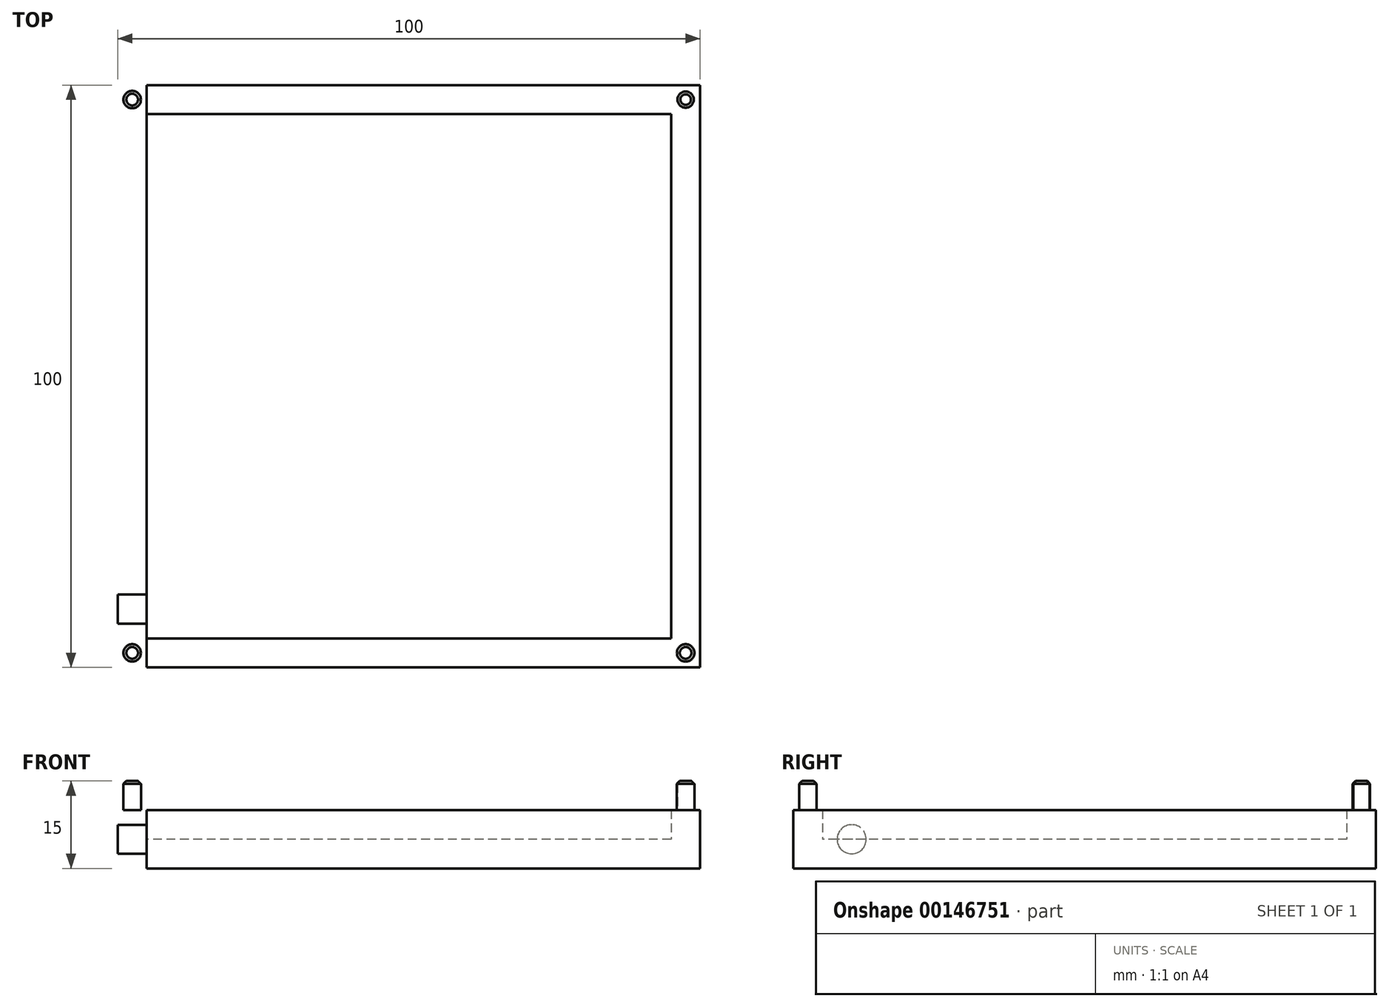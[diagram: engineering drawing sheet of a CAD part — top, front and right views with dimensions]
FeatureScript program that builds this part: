
annotation { "Feature Type Name" : "Feature", "Feature Type Description" : "" }
export const myFeature = defineFeature(function(context is Context, id is Id, definition is map)
    precondition{}
    {
        {
            var Q0;
            Q0=qCreatedBy(makeId("Top.planeOp"),FACE);
            var sketch = newSketch(context, id + "F0", { "sketchPlane" : qUnion([Q0])});
            skLineSegment(sketch, "E0.bottom", {"start": v(50, 50) * mm, "end": v(-50, 50) * mm});
            skLineSegment(sketch, "E0.top", {"start": v(50, -50) * mm, "end": v(-50, -50) * mm});
            skLineSegment(sketch, "E0.left", {"start": v(50, 50) * mm, "end": v(50, -50) * mm});
            skLineSegment(sketch, "E0.right", {"start": v(-50, 50) * mm, "end": v(-50, -50) * mm});
            skPoint(sketch, "E0.middle", {"position": v(0, 0) * mm});
            skSolve(sketch);
        }
        {
            var Q0;
            Q0=makeQuery(id+"F0.imprint","IMPRINT",FACE,{"disambiguationData":[TD([[makeQuery(id+"F0.imprint","IMPRINT",EDGE,{"derivedFrom":sQuery(id+"F0.wireOp",EDGE,"E0.bottom")}),1.0]])]});
            extrude(context, id + "F1", {"entities" : qUnion([Q0]), "depth" : 10 * mm});
        }
        {
            var Q0;
            Q0=makeQuery(id+"F1.opExtrude","CAP_FACE",FACE,{"disambiguationData":[OSD([sQuery(id+"F0.wireOp",EDGE,"E0.bottom"),sQuery(id+"F0.wireOp",EDGE,"E0.top"),sQuery(id+"F0.wireOp",EDGE,"E0.left"),sQuery(id+"F0.wireOp",EDGE,"E0.right")])],"isStart":false});
            shell(context, id + "F2", {"entities" : qUnion([Q0]), "thickness" : 5 * mm});
        }
        {
            var Q0;
            Q0=makeQuery(id+"F1.opExtrude","CAP_FACE",FACE,{"disambiguationData":[OSD([sQuery(id+"F0.wireOp",EDGE,"E0.bottom"),sQuery(id+"F0.wireOp",EDGE,"E0.top"),sQuery(id+"F0.wireOp",EDGE,"E0.left"),sQuery(id+"F0.wireOp",EDGE,"E0.right")])],"isStart":false});
            var sketch = newSketch(context, id + "F3", { "sketchPlane" : qUnion([Q0])});
            skLineSegment(sketch, "E1", {"start": v(-45, 45) * mm, "end": v(-50, 50) * mm, "construction": true});
            skLineSegment(sketch, "E2", {"start": v(-50, 50) * mm, "end": v(-47.5, 47.5) * mm, "construction": true});
            skCircle(sketch, "E3", {"center": v(-47.5, 47.5) * mm, "radius": 1.5 * mm, "construction": true});
            skCircle(sketch, "E4.1.0", {"center": v(47.5, 47.5) * mm, "radius": 1.5 * mm, "construction": true});
            skCircle(sketch, "E4.2.0", {"center": v(47.5, -47.5) * mm, "radius": 1.5 * mm, "construction": true});
            skCircle(sketch, "E4.3.0", {"center": v(-47.5, -47.5) * mm, "radius": 1.5 * mm, "construction": true});
            skPoint(sketch, "E4.center", {"position": v(0, 0) * mm});
            skLineSegment(sketch, "E4.anchor1", {"start": v(0, 0) * mm, "end": v(-47.5, 47.5) * mm, "construction": true});
            skLineSegment(sketch, "E4.anchor2", {"start": v(0, 0) * mm, "end": v(-47.5, -47.5) * mm, "construction": true});
            skCircle(sketch, "E5", {"center": v(-47.5, 47.5) * mm, "radius": 1.5 * mm});
            skCircle(sketch, "E6", {"center": v(47.5, 47.5) * mm, "radius": 1.4 * mm});
            skCircle(sketch, "E7", {"center": v(47.5, -47.5) * mm, "radius": 1.5 * mm});
            skCircle(sketch, "E8", {"center": v(-47.5, -47.5) * mm, "radius": 1.5 * mm});
            skSolve(sketch);
        }
        {
            var Q0;
            Q0=makeQuery(id+"F3.imprint","IMPRINT",FACE,{"disambiguationData":[TD([[makeQuery(id+"F3.imprint","IMPRINT",EDGE,{"derivedFrom":sQuery(id+"F3.wireOp",EDGE,"E8")}),1.0]])]});
            var Q1;
            Q1=makeQuery(id+"F3.imprint","IMPRINT",FACE,{"disambiguationData":[TD([[makeQuery(id+"F3.imprint","IMPRINT",EDGE,{"derivedFrom":sQuery(id+"F3.wireOp",EDGE,"E7")}),1.0]])]});
            var Q2;
            Q2=makeQuery(id+"F3.imprint","IMPRINT",FACE,{"disambiguationData":[TD([[makeQuery(id+"F3.imprint","IMPRINT",EDGE,{"derivedFrom":sQuery(id+"F3.wireOp",EDGE,"E6")}),1.0]])]});
            var Q3;
            Q3=makeQuery(id+"F3.imprint","IMPRINT",FACE,{"disambiguationData":[TD([[makeQuery(id+"F3.imprint","IMPRINT",EDGE,{"derivedFrom":sQuery(id+"F3.wireOp",EDGE,"E5")}),1.0]])]});
            extrude(context, id + "F4", {"entities" : qUnion([Q0, Q1, Q2, Q3]), "operationType" : NewBodyOperationType.ADD, "depth" : 5 * mm});
        }
        {
            var Q0;
            Q0=makeQuery(id+"F4.opExtrude","CAP_EDGE",EDGE,{"disambiguationData":[OSD([sQuery(id+"F3.wireOp",EDGE,"E6")])],"isStart":false});
            var Q1;
            Q1=makeQuery(id+"F4.opExtrude","CAP_EDGE",EDGE,{"disambiguationData":[OSD([sQuery(id+"F3.wireOp",EDGE,"E5")])],"isStart":false});
            var Q2;
            Q2=makeQuery(id+"F4.opExtrude","CAP_EDGE",EDGE,{"disambiguationData":[OSD([sQuery(id+"F3.wireOp",EDGE,"E8")])],"isStart":false});
            var Q3;
            Q3=makeQuery(id+"F4.opExtrude","CAP_EDGE",EDGE,{"disambiguationData":[OSD([sQuery(id+"F3.wireOp",EDGE,"E7")])],"isStart":false});
            chamfer(context, id + "F5", {"entities" : qUnion([Q0, Q1, Q2, Q3]), "width" : 0.5 * mm, "tangentPropagation" : true});
        }
        {
            var Q0;
            Q0=makeQuery(id+"F1.opExtrude","SWEPT_FACE",FACE,{"disambiguationData":[OSD([sQuery(id+"F0.wireOp",EDGE,"E0.right")])]});
            var sketch = newSketch(context, id + "F6", { "sketchPlane" : qUnion([Q0])});
            skLineSegment(sketch, "E9", {"start": v(0, 0) * mm, "end": v(0, 10) * mm, "construction": true});
            skLineSegment(sketch, "E10", {"start": v(0, 10) * mm, "end": v(0, 5) * mm, "construction": true});
            skLineSegment(sketch, "E11", {"start": v(0, 5) * mm, "end": v(-40, 5) * mm, "construction": true});
            skCircle(sketch, "E12", {"center": v(-40, 5) * mm, "radius": 2.5 * mm});
            skCircle(sketch, "E13.MirrorC", {"center": v(40, 5) * mm, "radius": 2.5 * mm});
            skSolve(sketch);
        }
        {
            var Q0;
            Q0=makeQuery(id+"F6.imprint","IMPRINT",FACE,{"disambiguationData":[TD([[makeQuery(id+"F6.imprint","IMPRINT",EDGE,{"derivedFrom":sQuery(id+"F6.wireOp",EDGE,"E13.MirrorC")}),-1.0]])]});
            var Q1;
            Q1=makeQuery(id+"F6.imprint","IMPRINT",FACE,{"disambiguationData":[TD([[makeQuery(id+"F6.imprint","IMPRINT",EDGE,{"derivedFrom":sQuery(id+"F6.wireOp",EDGE,"E12")}),1.0]])]});
            extrude(context, id + "F7", {"entities" : qUnion([Q0, Q1]), "operationType" : NewBodyOperationType.REMOVE, "oppositeDirection" : true, "depth" : 5 * mm});
        }
    });
